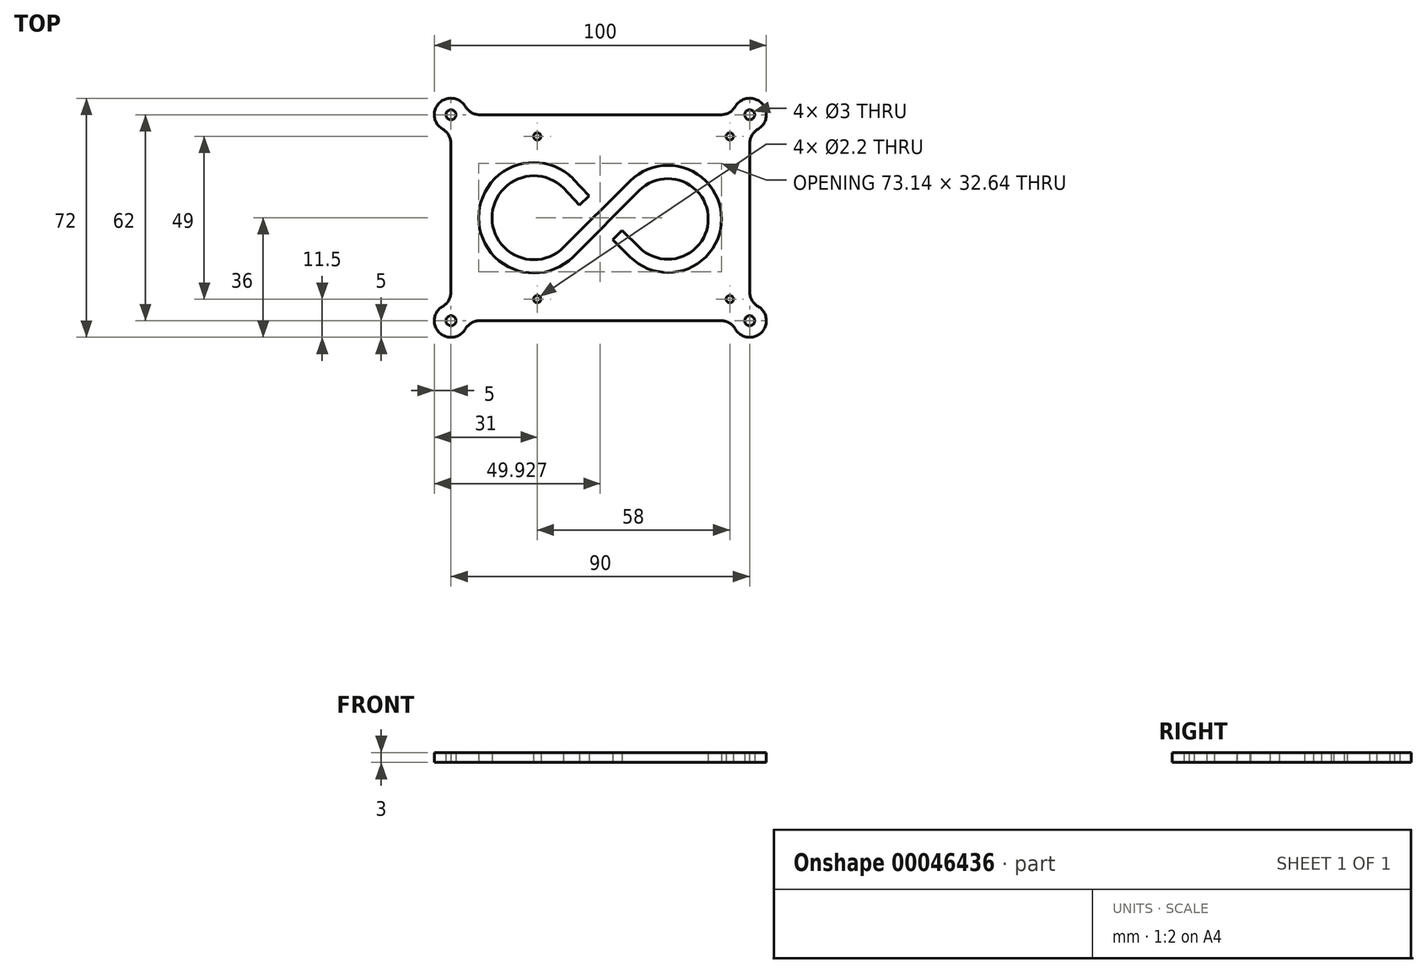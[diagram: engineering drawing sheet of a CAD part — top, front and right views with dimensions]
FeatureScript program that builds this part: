
annotation { "Feature Type Name" : "Feature", "Feature Type Description" : "" }
export const myFeature = defineFeature(function(context is Context, id is Id, definition is map)
    precondition{}
    {
        {
            var Q0;
            Q0=qCreatedBy(makeId("Top.planeOp"),FACE);
            var sketch = newSketch(context, id + "F0", { "sketchPlane" : qUnion([Q0])});
            skLineSegment(sketch, "E0.bottom", {"start": v(45, -31) * mm, "end": v(-45, -31) * mm});
            skLineSegment(sketch, "E0.top", {"start": v(45, 31) * mm, "end": v(-45, 31) * mm});
            skLineSegment(sketch, "E0.left", {"start": v(45, -31) * mm, "end": v(45, 31) * mm});
            skLineSegment(sketch, "E0.right", {"start": v(-45, -31) * mm, "end": v(-45, 31) * mm});
            skPoint(sketch, "E0.middle", {"position": v(0, 0) * mm});
            skCircle(sketch, "E1", {"center": v(45, 31) * mm, "radius": 5 * mm});
            skCircle(sketch, "E2", {"center": v(45, -31) * mm, "radius": 5 * mm});
            skCircle(sketch, "E3", {"center": v(-45, 31) * mm, "radius": 5 * mm});
            skCircle(sketch, "E4", {"center": v(-45, -31) * mm, "radius": 5 * mm});
            skCircle(sketch, "E5", {"center": v(45, 31) * mm, "radius": 1.5 * mm});
            skCircle(sketch, "E6", {"center": v(45, -31) * mm, "radius": 1.5 * mm});
            skCircle(sketch, "E7", {"center": v(-45, -31) * mm, "radius": 1.5 * mm});
            skCircle(sketch, "E8", {"center": v(-45, 31) * mm, "radius": 1.5 * mm});
            skPoint(sketch, "E9.third.point", {"position": v(34.14, 0) * mm});
            skPoint(sketch, "E9.third.point.positionSnap0", {"position": v(10, 0) * mm});
            skArc(sketch, "E10", {"start": v(10.35, 9.65) * mm, "mid": v(34.5, -0.35) * mm, "end": v(10.35, -10.35) * mm});
            skArc(sketch, "E11", {"start": v(-9.65, -10.35) * mm, "mid": v(-34.64, 0) * mm, "end": v(-9.65, 10.35) * mm});
            skLineSegment(sketch, "E12", {"start": v(-9.65, -10.35) * mm, "end": v(10.35, 9.65) * mm});
            skPoint(sketch, "E13", {"position": v(5.18, -5.18) * mm});
            skPoint(sketch, "E14", {"position": v(-4.82, 5.18) * mm});
            skLineSegment(sketch, "E15", {"start": v(-9.65, 10.35) * mm, "end": v(-4.82, 5.18) * mm});
            skLineSegment(sketch, "E16", {"start": v(10.35, -10.35) * mm, "end": v(5.18, -5.18) * mm});
            skArc(sketch, "E17.0.startCap", {"start": v(11.77, 8.23) * mm, "mid": v(8.94, 8.23) * mm, "end": v(8.94, 11.06) * mm});
            skArc(sketch, "E17.0.endCap", {"start": v(8.94, -11.77) * mm, "mid": v(8.94, -8.94) * mm, "end": v(11.77, -8.94) * mm});
            skArc(sketch, "E17.0.left", {"start": v(8.94, 11.06) * mm, "mid": v(36.5, -0.35) * mm, "end": v(8.94, -11.77) * mm});
            skArc(sketch, "E17.0.right", {"start": v(11.77, 8.23) * mm, "mid": v(32.5, -0.35) * mm, "end": v(11.77, -8.94) * mm});
            skArc(sketch, "E17.1.startCap", {"start": v(11.77, -8.94) * mm, "mid": v(11.77, -11.77) * mm, "end": v(8.94, -11.77) * mm});
            skLineSegment(sketch, "E17.1.left", {"start": v(8.94, -11.77) * mm, "end": v(3.76, -6.6) * mm});
            skLineSegment(sketch, "E17.1.right", {"start": v(11.77, -8.94) * mm, "end": v(6.6, -3.76) * mm});
            skArc(sketch, "E17.2.startCap", {"start": v(-8.23, -11.77) * mm, "mid": v(-11.06, -11.77) * mm, "end": v(-11.06, -8.94) * mm});
            skArc(sketch, "E17.2.endCap", {"start": v(8.94, 11.06) * mm, "mid": v(11.77, 11.06) * mm, "end": v(11.77, 8.23) * mm});
            skLineSegment(sketch, "E17.2.left", {"start": v(-11.06, -8.94) * mm, "end": v(8.94, 11.06) * mm});
            skLineSegment(sketch, "E17.2.right", {"start": v(-8.23, -11.77) * mm, "end": v(11.77, 8.23) * mm});
            skArc(sketch, "E17.3.startCap", {"start": v(-11.06, -8.94) * mm, "mid": v(-8.23, -8.94) * mm, "end": v(-8.23, -11.77) * mm});
            skArc(sketch, "E17.3.endCap", {"start": v(-8.23, 11.77) * mm, "mid": v(-8.23, 8.94) * mm, "end": v(-11.06, 8.94) * mm});
            skArc(sketch, "E17.3.left", {"start": v(-8.23, -11.77) * mm, "mid": v(-36.64, 0) * mm, "end": v(-8.23, 11.77) * mm});
            skArc(sketch, "E17.3.right", {"start": v(-11.06, -8.94) * mm, "mid": v(-32.64, 0) * mm, "end": v(-11.06, 8.94) * mm});
            skArc(sketch, "E17.4.startCap", {"start": v(-11.1, 9) * mm, "mid": v(-11, 11.82) * mm, "end": v(-8.18, 11.72) * mm});
            skLineSegment(sketch, "E17.4.left", {"start": v(-8.18, 11.72) * mm, "end": v(-3.36, 6.54) * mm});
            skLineSegment(sketch, "E17.4.right", {"start": v(-11.1, 9) * mm, "end": v(-6.29, 3.81) * mm});
            skLineSegment(sketch, "E18", {"start": v(-6.29, 3.81) * mm, "end": v(-3.36, 6.54) * mm});
            skLineSegment(sketch, "E19", {"start": v(3.76, -6.6) * mm, "end": v(6.6, -3.76) * mm});
            skSolve(sketch);
        }
        {
            var Q0;
            Q0=qSketchRegion(id+"F0",true);
            extrude(context, id + "F1", {"entities" : qUnion([Q0]), "depth" : 3 * mm});
        }
        {
            var Q0;
            Q0=makeQuery(id+"F1.opExtrude","SWEPT_EDGE",EDGE,{"disambiguationData":[OSD([sQuery(id+"F0.wireOp",EDGE,"E0.bottom"),sQuery(id+"F0.wireOp",EDGE,"E4")])]});
            var Q1;
            Q1=makeQuery(id+"F1.opExtrude","SWEPT_EDGE",EDGE,{"disambiguationData":[OSD([sQuery(id+"F0.wireOp",EDGE,"E0.left"),sQuery(id+"F0.wireOp",EDGE,"E1")])]});
            var Q2;
            Q2=makeQuery(id+"F1.opExtrude","SWEPT_EDGE",EDGE,{"disambiguationData":[OSD([sQuery(id+"F0.wireOp",EDGE,"E0.bottom"),sQuery(id+"F0.wireOp",EDGE,"E2")])]});
            var Q3;
            Q3=makeQuery(id+"F1.opExtrude","SWEPT_EDGE",EDGE,{"disambiguationData":[OSD([sQuery(id+"F0.wireOp",EDGE,"E0.right"),sQuery(id+"F0.wireOp",EDGE,"E4")])]});
            var Q4;
            Q4=makeQuery(id+"F1.opExtrude","SWEPT_EDGE",EDGE,{"disambiguationData":[OSD([sQuery(id+"F0.wireOp",EDGE,"E0.right"),sQuery(id+"F0.wireOp",EDGE,"E3")])]});
            var Q5;
            Q5=makeQuery(id+"F1.opExtrude","SWEPT_EDGE",EDGE,{"disambiguationData":[OSD([sQuery(id+"F0.wireOp",EDGE,"E0.top"),sQuery(id+"F0.wireOp",EDGE,"E3")])]});
            var Q6;
            Q6=makeQuery(id+"F1.opExtrude","SWEPT_EDGE",EDGE,{"disambiguationData":[OSD([sQuery(id+"F0.wireOp",EDGE,"E0.top"),sQuery(id+"F0.wireOp",EDGE,"E1")])]});
            var Q7;
            Q7=makeQuery(id+"F1.opExtrude","SWEPT_EDGE",EDGE,{"disambiguationData":[OSD([sQuery(id+"F0.wireOp",EDGE,"E0.left"),sQuery(id+"F0.wireOp",EDGE,"E2")])]});
            fillet(context, id + "F2", {"entities" : qUnion([Q0, Q1, Q2, Q3, Q4, Q5, Q6, Q7]), "radius" : 5 * mm, "tangentPropagation" : true, "allowEdgeOverflow" : false});
        }
        {
            var Q0;
            Q0=makeQuery(id+"F1.opExtrude","CAP_FACE",FACE,{"disambiguationData":[OSD([sQuery(id+"F0.wireOp",EDGE,"E0.bottom"),sQuery(id+"F0.wireOp",EDGE,"E0.top"),sQuery(id+"F0.wireOp",EDGE,"E0.left"),sQuery(id+"F0.wireOp",EDGE,"E0.right"),sQuery(id+"F0.wireOp",EDGE,"E1"),sQuery(id+"F0.wireOp",EDGE,"E2"),sQuery(id+"F0.wireOp",EDGE,"E3"),sQuery(id+"F0.wireOp",EDGE,"E4"),sQuery(id+"F0.wireOp",EDGE,"E5"),sQuery(id+"F0.wireOp",EDGE,"E6"),sQuery(id+"F0.wireOp",EDGE,"E7"),sQuery(id+"F0.wireOp",EDGE,"E8"),sQuery(id+"F0.wireOp",EDGE,"E17.0.left"),sQuery(id+"F0.wireOp",EDGE,"E17.0.right"),sQuery(id+"F0.wireOp",EDGE,"E17.1.left"),sQuery(id+"F0.wireOp",EDGE,"E17.1.right"),sQuery(id+"F0.wireOp",EDGE,"E17.2.left"),sQuery(id+"F0.wireOp",EDGE,"E17.2.right"),sQuery(id+"F0.wireOp",EDGE,"E17.3.left"),sQuery(id+"F0.wireOp",EDGE,"E17.3.right"),sQuery(id+"F0.wireOp",EDGE,"E17.4.startCap"),sQuery(id+"F0.wireOp",EDGE,"E17.4.left"),sQuery(id+"F0.wireOp",EDGE,"E17.4.right"),sQuery(id+"F0.wireOp",EDGE,"E18"),sQuery(id+"F0.wireOp",EDGE,"E19")])],"isStart":false});
            var sketch = newSketch(context, id + "F3", { "sketchPlane" : qUnion([Q0])});
            skPoint(sketch, "E20", {"position": v(39, 24.5) * mm});
            skPoint(sketch, "E21", {"position": v(39, -24.5) * mm});
            skPoint(sketch, "E22", {"position": v(-19, 24.5) * mm});
            skPoint(sketch, "E23", {"position": v(-19, -24.5) * mm});
            skSolve(sketch);
        }
        {
            var Q0;
            Q0=sQuery(id+"F3.wireOp",VERTEX,"E22");
            var Q1;
            Q1=sQuery(id+"F3.wireOp",VERTEX,"E20");
            var Q2;
            Q2=sQuery(id+"F3.wireOp",VERTEX,"E21");
            var Q3;
            Q3=sQuery(id+"F3.wireOp",VERTEX,"E23");
            var Q4;
            Q4=makeQuery(id+"F1.opExtrude","SWEPT_BODY",BODY,{"disambiguationData":[OSD([sQuery(id+"F0.wireOp",EDGE,"E0.bottom"),sQuery(id+"F0.wireOp",EDGE,"E0.top"),sQuery(id+"F0.wireOp",EDGE,"E0.left"),sQuery(id+"F0.wireOp",EDGE,"E0.right"),sQuery(id+"F0.wireOp",EDGE,"E1"),sQuery(id+"F0.wireOp",EDGE,"E2"),sQuery(id+"F0.wireOp",EDGE,"E3"),sQuery(id+"F0.wireOp",EDGE,"E4"),sQuery(id+"F0.wireOp",EDGE,"E5"),sQuery(id+"F0.wireOp",EDGE,"E6"),sQuery(id+"F0.wireOp",EDGE,"E7"),sQuery(id+"F0.wireOp",EDGE,"E8"),sQuery(id+"F0.wireOp",EDGE,"E17.0.left"),sQuery(id+"F0.wireOp",EDGE,"E17.0.right"),sQuery(id+"F0.wireOp",EDGE,"E17.1.left"),sQuery(id+"F0.wireOp",EDGE,"E17.1.right"),sQuery(id+"F0.wireOp",EDGE,"E17.2.left"),sQuery(id+"F0.wireOp",EDGE,"E17.2.right"),sQuery(id+"F0.wireOp",EDGE,"E17.3.left"),sQuery(id+"F0.wireOp",EDGE,"E17.3.right"),sQuery(id+"F0.wireOp",EDGE,"E17.4.startCap"),sQuery(id+"F0.wireOp",EDGE,"E17.4.left"),sQuery(id+"F0.wireOp",EDGE,"E17.4.right"),sQuery(id+"F0.wireOp",EDGE,"E18"),sQuery(id+"F0.wireOp",EDGE,"E19")])]});
            hole(context, id + "F4", {"style" : HoleStyle.SIMPLE, "endStyle" : HoleEndStyle.THROUGH, "holeDiameter" : 2.2 * mm, "locations" : qUnion([Q0, Q1, Q2, Q3]), "scope" : qUnion([Q4]), "tappedDepth" : 12 * mm, "tapClearance" : 3, "startStyle" : HoleStartStyle.PART});
        }
    });
